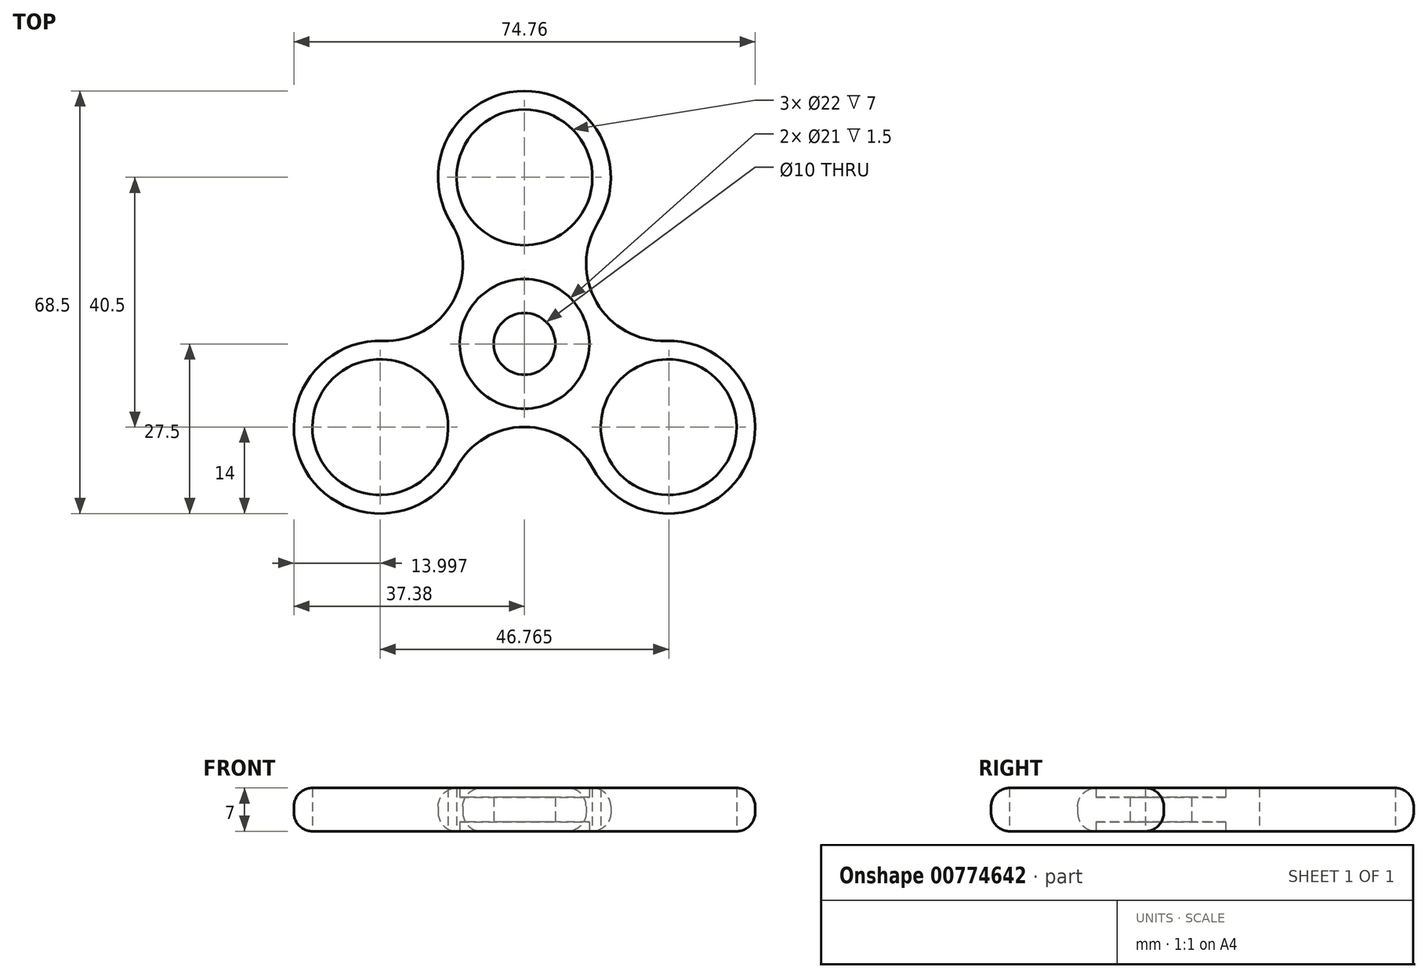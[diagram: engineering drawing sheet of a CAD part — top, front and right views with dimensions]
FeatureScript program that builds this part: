
annotation { "Feature Type Name" : "Feature", "Feature Type Description" : "" }
export const myFeature = defineFeature(function(context is Context, id is Id, definition is map)
    precondition{}
    {
        {
            var Q0;
            Q0=qCreatedBy(makeId("Top.planeOp"),FACE);
            var sketch = newSketch(context, id + "F0", { "sketchPlane" : qUnion([Q0])});
            skCircle(sketch, "E0", {"center": v(0, 0) * mm, "radius": 5 * mm});
            skCircle(sketch, "E1", {"center": v(0, 0) * mm, "radius": 4.25 * mm});
            skCircle(sketch, "E2", {"center": v(0, 27) * mm, "radius": 11 * mm});
            skLineSegment(sketch, "E3", {"start": v(0, 0) * mm, "end": v(0, 27) * mm});
            skCircle(sketch, "E4", {"center": v(-23.38, -13.5) * mm, "radius": 11 * mm});
            skCircle(sketch, "E5", {"center": v(23.38, -13.5) * mm, "radius": 11 * mm});
            skArc(sketch, "E6", {"start": v(-22.91, 0.5) * mm, "mid": v(-11.67, 6.73) * mm, "end": v(-11.88, 19.6) * mm});
            skArc(sketch, "E7.1.0", {"start": v(11.03, -20.09) * mm, "mid": v(0, -13.47) * mm, "end": v(-11.03, -20.09) * mm});
            skArc(sketch, "E7.2.0", {"start": v(11.88, 19.6) * mm, "mid": v(11.67, 6.73) * mm, "end": v(22.91, 0.5) * mm});
            skArc(sketch, "E8", {"start": v(-22.91, 0.5) * mm, "mid": v(-35.5, -20.5) * mm, "end": v(-11.03, -20.09) * mm});
            skArc(sketch, "E9", {"start": v(11.88, 19.6) * mm, "mid": v(0, 41) * mm, "end": v(-11.88, 19.6) * mm});
            skArc(sketch, "E10", {"start": v(11.03, -20.09) * mm, "mid": v(35.5, -20.5) * mm, "end": v(22.91, 0.5) * mm});
            skCircle(sketch, "E11", {"center": v(0, 0) * mm, "radius": 13.5 * mm});
            skCircle(sketch, "E12", {"center": v(0, 0) * mm, "radius": 10.5 * mm});
            skSolve(sketch);
        }
        {
            var Q0;
            Q0=makeQuery(id+"F0.imprint","IMPRINT",FACE,{"disambiguationData":[TD([[makeQuery(id+"F0.imprint","IMPRINT",EDGE,{"derivedFrom":sQuery(id+"F0.wireOp",EDGE,"E5")}),-1.0]])]});
            var Q1;
            Q1=makeQuery(id+"F0.imprint","IMPRINT",FACE,{"disambiguationData":[TD([[makeQuery(id+"F0.imprint","IMPRINT",EDGE,{"derivedFrom":sQuery(id+"F0.wireOp",EDGE,"E4")}),-1.0]])]});
            var Q2;
            Q2=makeQuery(id+"F0.imprint","IMPRINT",FACE,{"disambiguationData":[TD([[makeQuery(id+"F0.imprint","IMPRINT",EDGE,{"derivedFrom":sQuery(id+"F0.wireOp",EDGE,"E2")}),-1.0]])]});
            var Q3;
            Q3=makeQuery(id+"F0.imprint","IMPRINT",FACE,{"disambiguationData":[TD([[makeQuery(id+"F0.imprint","IMPRINT",EDGE,{"derivedFrom":sQuery(id+"F0.wireOp",EDGE,"E12")}),-1.0]])]});
            extrude(context, id + "F1", {"entities" : qUnion([Q0, Q1, Q2, Q3]), "endBound" : BoundingType.SYMMETRIC, "depth" : 7 * mm, "offsetDistance" : 25 * mm});
        }
        {
            var Q0;
            Q0=makeQuery(id+"F1.opExtrude","CAP_EDGE",EDGE,{"disambiguationData":[OSD([sQuery(id+"F0.wireOp",EDGE,"E7.1.0")])],"isStart":false});
            var Q1;
            Q1=makeQuery(id+"F1.opExtrude","SWEPT_FACE",FACE,{"disambiguationData":[OSD([sQuery(id+"F0.wireOp",EDGE,"E7.1.0")])]});
            fillet(context, id + "F2", {"entities" : qUnion([Q0, Q1]), "radius" : 3 * mm, "tangentPropagation" : true, "allowEdgeOverflow" : false});
        }
        {
            var Q0;
            Q0=makeQuery(id+"F0.imprint","IMPRINT",FACE,{"disambiguationData":[TD([[makeQuery(id+"F0.imprint","IMPRINT",EDGE,{"derivedFrom":sQuery(id+"F0.wireOp",EDGE,"E0")}),-1.0]])]});
            extrude(context, id + "F3", {"entities" : qUnion([Q0]), "operationType" : NewBodyOperationType.ADD, "endBound" : BoundingType.SYMMETRIC, "depth" : 4 * mm, "offsetDistance" : 25 * mm});
        }
    });
